# Revit family: LP7-WM
name_source: partatom
category: Lighting Fixtures
revit_build: Autodesk Revit 2013 (Build: 20130531_2115(x64)
units: mm (PartAtom-declared; Revit-internal decimal feet)

## types (1)
- LP7
    Apparent Load = 40 VA
    Assembly Code = D5020210
    Color Filter = 16777215
    Description = Plank 7'' LED Wall Mount
    Dimming Lamp Color Temperature Shift = <None>
    Emit Shape Visible in Rendering = No
    Emit from Rectangle Length = 3 "
    Emit from Rectangle Width = 48 "
    Glass = Hubbell - White Glass
    Housing Material = Hubbell - White
    Lamp = LED
    Load Classification = Lighting
    Manufacturer = Alera Lighting
    Model = LP7-WM
    Photometric Notes = IES files download on Photometric Web Link
    Photometric Web File = generic.ies
    Photometric Web Link = https://www.hubbell.com
    Power Factor = 1
    Product Documentation Link = https://hubbellcdn.com
    Product Page URL = https://www.hubbell.com
    Row Option = LP7 : 4'
    Tilt Angle = 90.00°
    URL = https://www.hubbell.com
    Voltage = 120 V
    Watts = 40 W

## geometry (parser evidence)
native form markers: Blend x8, Sweep x2
no freeform markers — native parametric forms only
